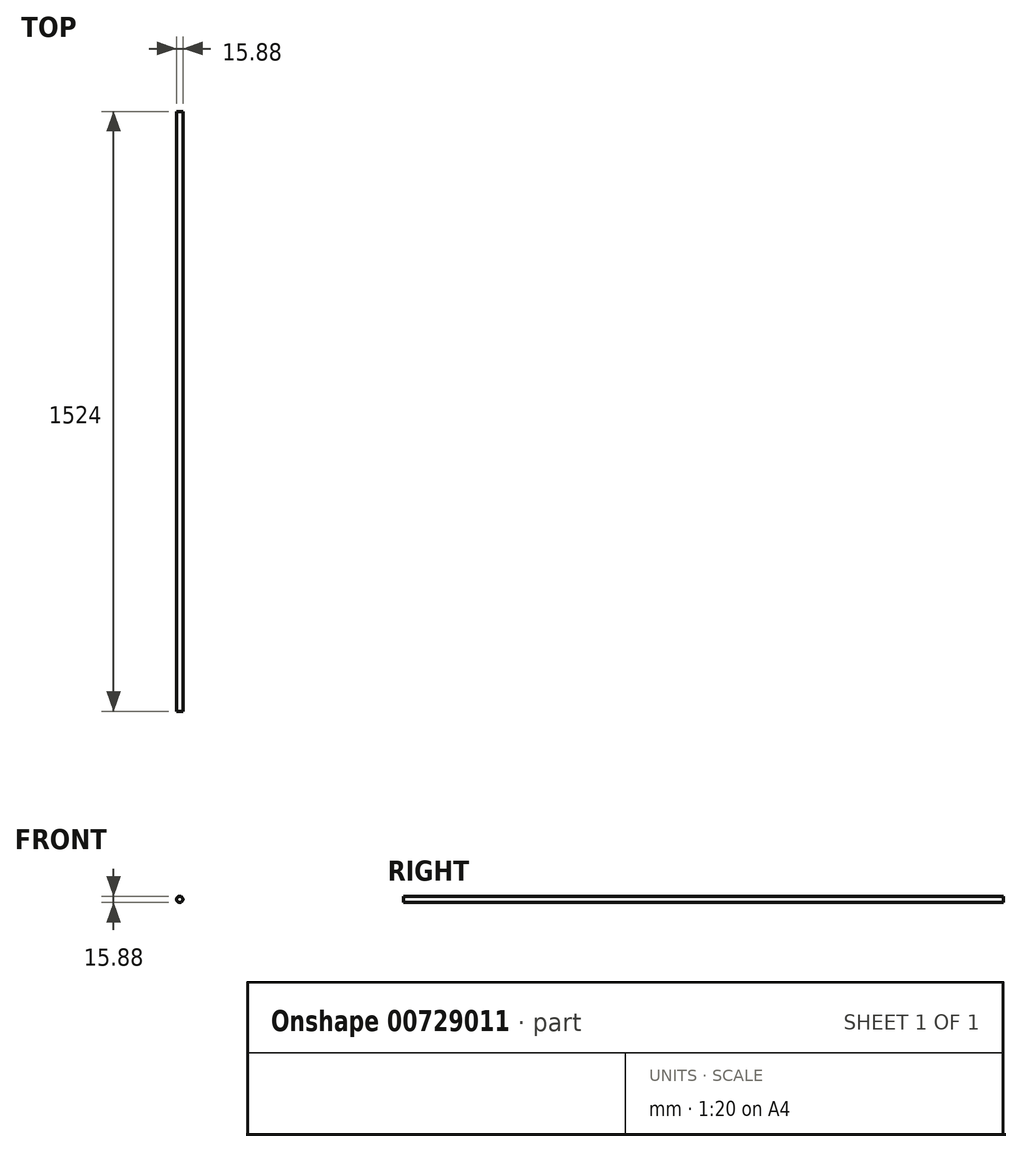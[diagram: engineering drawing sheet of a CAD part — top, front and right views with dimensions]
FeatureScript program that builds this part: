
annotation { "Feature Type Name" : "Feature", "Feature Type Description" : "" }
export const myFeature = defineFeature(function(context is Context, id is Id, definition is map)
    precondition{}
    {
        {
            var Q0;
            Q0=qCreatedBy(makeId("Front.planeOp"),FACE);
            var sketch = newSketch(context, id + "F0", { "sketchPlane" : qUnion([Q0])});
            skCircle(sketch, "E0", {"center": v(0, 0) * mm, "radius": 7.94 * mm});
            skSolve(sketch);
        }
        {
            var Q0;
            Q0 = qSketchRegion(id + "F0", true);
            extrude(context, id + "F1", {"entities" : qUnion([Q0]), "depth" : 1524 * mm, "offsetDistance" : 25.4 * mm});
        }
    });
